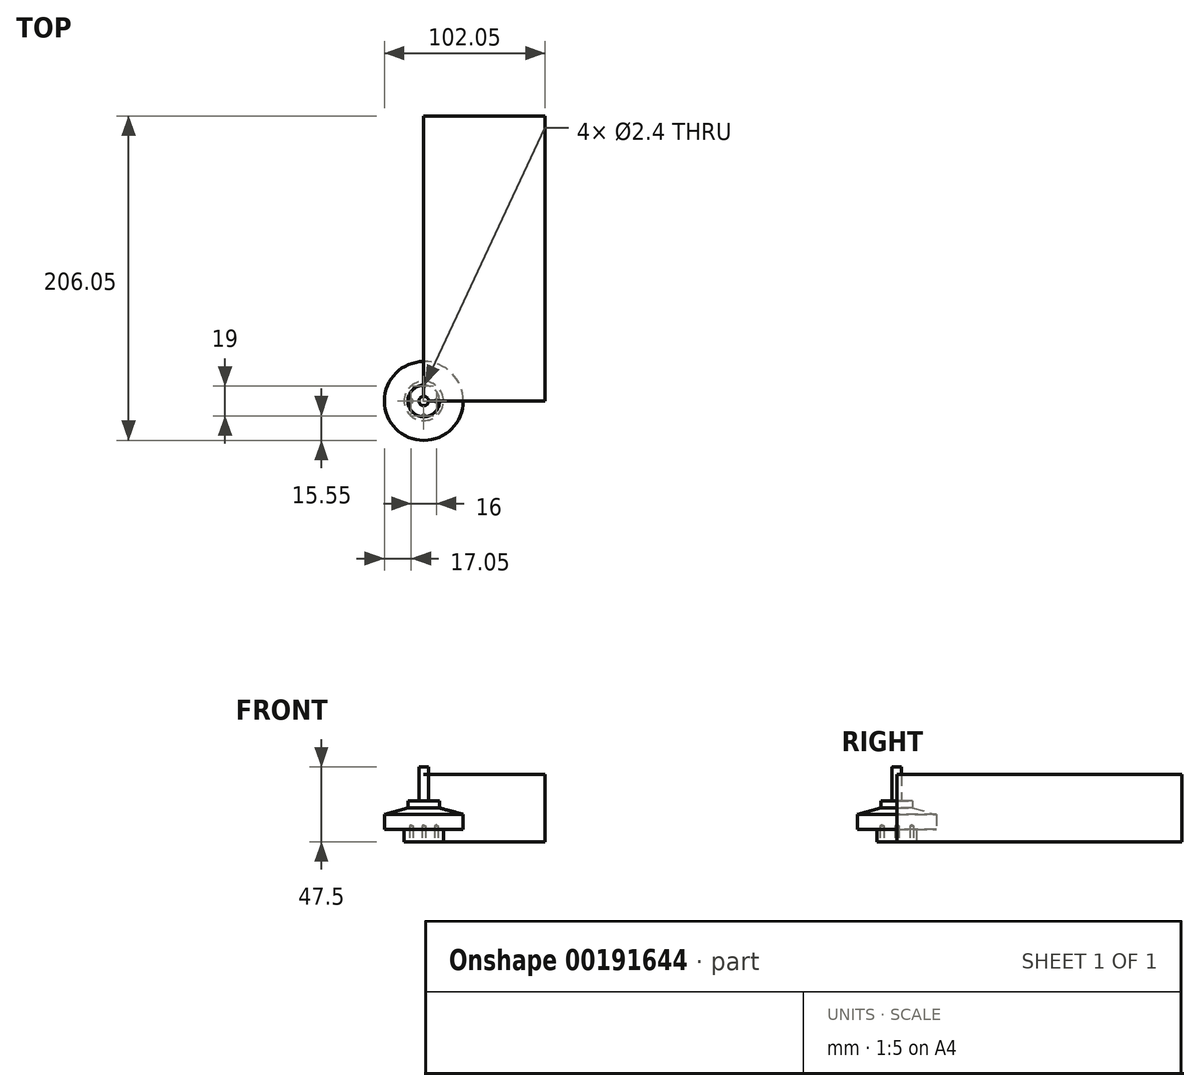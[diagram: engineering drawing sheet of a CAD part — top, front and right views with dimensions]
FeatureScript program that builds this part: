
annotation { "Feature Type Name" : "Feature", "Feature Type Description" : "" }
export const myFeature = defineFeature(function(context is Context, id is Id, definition is map)
    precondition{}
    {
        {
            var Q0;
            Q0=qCreatedBy(makeId("Top.planeOp"),FACE);
            var sketch = newSketch(context, id + "F0", { "sketchPlane" : qUnion([Q0])});
            skCircle(sketch, "E0", {"center": v(0, 0) * mm, "radius": 12.5 * mm});
            skSolve(sketch);
        }
        {
            var Q0;
            Q0=makeQuery(id+"F0.imprint","IMPRINT",FACE,{"disambiguationData":[TD([[makeQuery(id+"F0.imprint","IMPRINT",EDGE,{"derivedFrom":sQuery(id+"F0.wireOp",EDGE,"E0")}),1.0]])]});
            extrude(context, id + "F1", {"entities" : qUnion([Q0]), "depth" : 8 * mm});
        }
        {
            var Q0;
            Q0=makeQuery(id+"F1.opExtrude","CAP_FACE",FACE,{"disambiguationData":[OSD([sQuery(id+"F0.wireOp",EDGE,"E0")])],"isStart":false});
            var sketch = newSketch(context, id + "F2", { "sketchPlane" : qUnion([Q0])});
            skCircle(sketch, "E1", {"center": v(0, 0) * mm, "radius": 25.05 * mm});
            skSolve(sketch);
        }
        {
            var Q0;
            Q0 = qSketchRegion(id + "F2", true);
            extrude(context, id + "F3", {"entities" : qUnion([Q0]), "operationType" : NewBodyOperationType.ADD, "depth" : 13.5 * mm});
        }
        {
            var Q0;
            Q0=makeQuery(id+"F3.opExtrude","CAP_EDGE",EDGE,{"disambiguationData":[OSD([sQuery(id+"F2.wireOp",EDGE,"E1")])],"isStart":false});
            chamfer(context, id + "F4", {"entities" : qUnion([Q0]), "chamferType" : ChamferType.TWO_OFFSETS, "width1" : 15 * mm, "oppositeDirection" : false, "width2" : 4 * mm, "tangentPropagation" : true});
        }
        {
            var Q0;
            Q0=makeQuery(id+"F1.opExtrude","CAP_FACE",FACE,{"disambiguationData":[OSD([sQuery(id+"F0.wireOp",EDGE,"E0")])],"isStart":true});
            var sketch = newSketch(context, id + "F5", { "sketchPlane" : qUnion([Q0])});
            skPoint(sketch, "E2", {"position": v(-8, 0) * mm});
            skPoint(sketch, "E3", {"position": v(8, 0) * mm});
            skPoint(sketch, "E4", {"position": v(0, 9.5) * mm});
            skPoint(sketch, "E5", {"position": v(0, -9.5) * mm});
            skSolve(sketch);
        }
        {
            var Q0;
            Q0=sQuery(id+"F5.wireOp",VERTEX,"E4");
            var Q1;
            Q1=sQuery(id+"F5.wireOp",VERTEX,"E5");
            var Q2;
            Q2=sQuery(id+"F5.wireOp",VERTEX,"E3");
            var Q3;
            Q3=sQuery(id+"F5.wireOp",VERTEX,"E2");
            var Q4;
            Q4=makeQuery(id+"F1.opExtrude","SWEPT_BODY",BODY,{"disambiguationData":[OSD([sQuery(id+"F0.wireOp",EDGE,"E0")])]});
            hole(context, id + "F6", {"style" : HoleStyle.SIMPLE, "endStyle" : HoleEndStyle.BLIND, "standardTappedOrClearance" : lookupTablePath({ "standard" : "ISO", "engagement" : "75%", "pitch" : "0.6 mm", "size" : "M3", "type" : "Tapped" }), "standardBlindInLast" : lookupTablePath({ "standard" : "ISO", "engagement" : "75%", "pitch" : "0.6 mm", "size" : "M3", "type" : "Tapped" }), "holeDiameter" : 2.4 * mm, "holeDepth" : 10 * mm, "locations" : qUnion([Q0, Q1, Q2, Q3]), "scope" : qUnion([Q4])});
        }
        {
            var Q0;
            Q0=makeQuery(id+"F3.opExtrude","CAP_FACE",FACE,{"disambiguationData":[OSD([sQuery(id+"F2.wireOp",EDGE,"E1")])],"isStart":false});
            var sketch = newSketch(context, id + "F7", { "sketchPlane" : qUnion([Q0])});
            skCircle(sketch, "E6", {"center": v(0, 0) * mm, "radius": 10 * mm});
            skSolve(sketch);
        }
        {
            var Q0;
            Q0 = qSketchRegion(id + "F7", true);
            extrude(context, id + "F8", {"entities" : qUnion([Q0]), "operationType" : NewBodyOperationType.ADD, "depth" : 4.5 * mm});
        }
        {
            var Q0;
            Q0=makeQuery(id+"F8.opExtrude","CAP_FACE",FACE,{"disambiguationData":[OSD([sQuery(id+"F7.wireOp",EDGE,"E6")])],"isStart":false});
            var sketch = newSketch(context, id + "F9", { "sketchPlane" : qUnion([Q0])});
            skCircle(sketch, "E7", {"center": v(0, 0) * mm, "radius": 3 * mm});
            skSolve(sketch);
        }
        {
            var Q0;
            Q0 = qSketchRegion(id + "F9", true);
            extrude(context, id + "F10", {"entities" : qUnion([Q0]), "operationType" : NewBodyOperationType.ADD, "depth" : 21.5 * mm});
        }
        {
            var Q0;
            Q0=qCreatedBy(makeId("Top.planeOp"),FACE);
            var sketch = newSketch(context, id + "F11", { "sketchPlane" : qUnion([Q0])});
            skLineSegment(sketch, "E8.bottom", {"start": v(0, 0) * mm, "end": v(77, 0) * mm});
            skLineSegment(sketch, "E8.top", {"start": v(0, 181) * mm, "end": v(77, 181) * mm});
            skLineSegment(sketch, "E8.left", {"start": v(0, 0) * mm, "end": v(0, 181) * mm});
            skLineSegment(sketch, "E8.right", {"start": v(77, 0) * mm, "end": v(77, 181) * mm});
            skSolve(sketch);
        }
        {
            var Q0;
            Q0 = qSketchRegion(id + "F11", true);
            extrude(context, id + "F12", {"entities" : qUnion([Q0]), "depth" : 43 * mm});
        }
    });
